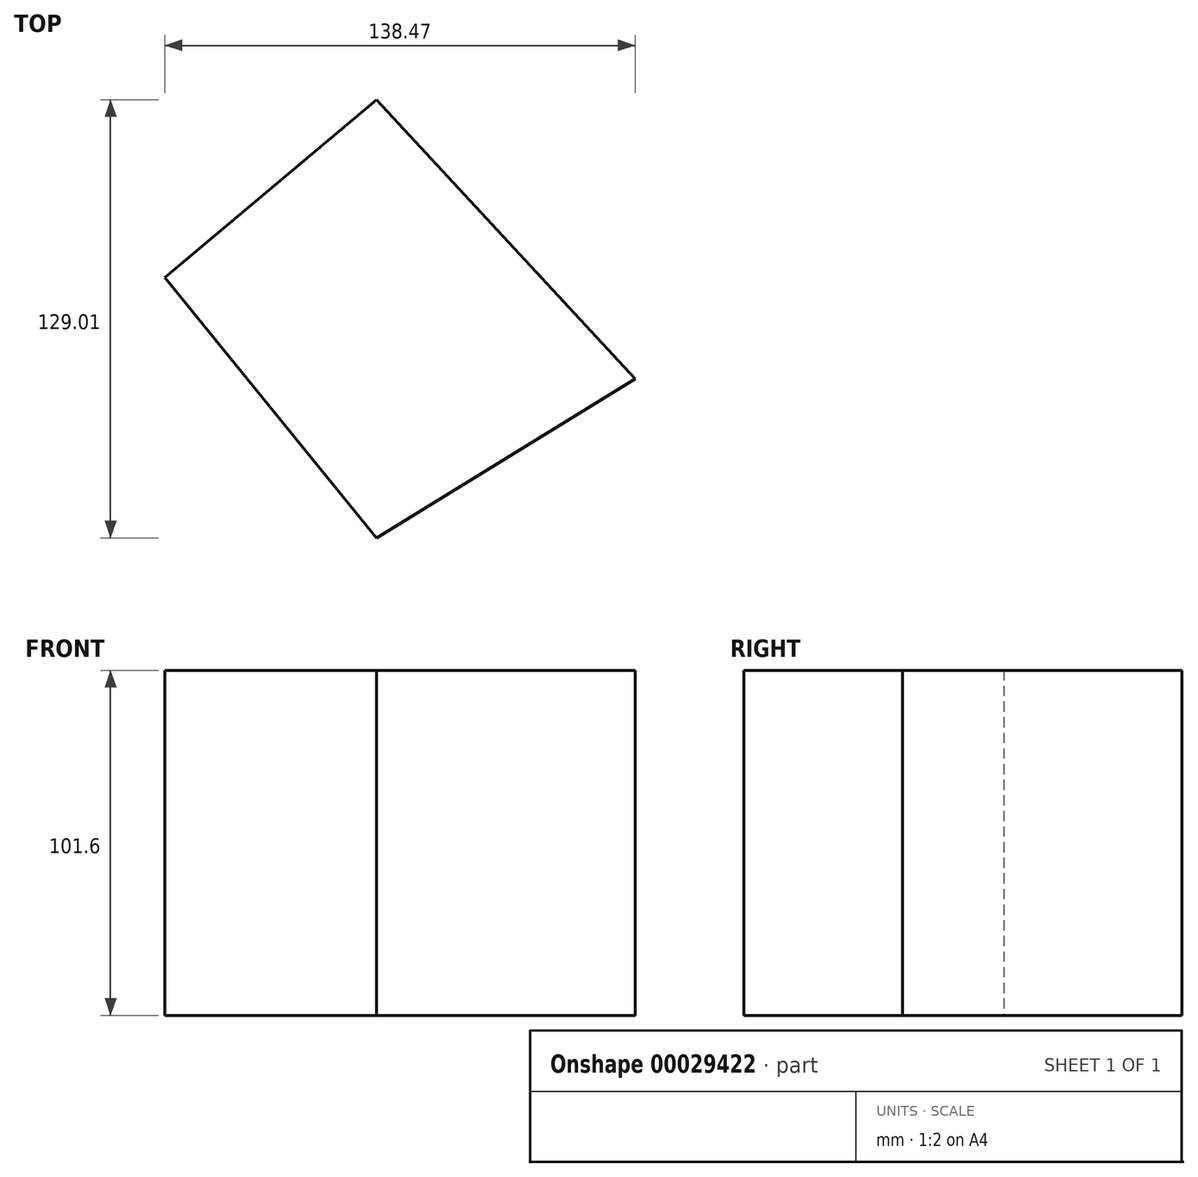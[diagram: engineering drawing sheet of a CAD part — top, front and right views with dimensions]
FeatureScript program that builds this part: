
annotation { "Feature Type Name" : "Feature", "Feature Type Description" : "" }
export const myFeature = defineFeature(function(context is Context, id is Id, definition is map)
    precondition{}
    {
        {
            var Q0;
            Q0=qCreatedBy(makeId("Top.planeOp"),FACE);
            var sketch = newSketch(context, id + "F0", { "sketchPlane" : qUnion([Q0])});
            skLineSegment(sketch, "E0", {"start": v(-62.28, 0) * mm, "end": v(0, 52.33) * mm});
            skLineSegment(sketch, "E1", {"start": v(0, 52.33) * mm, "end": v(76.19, -29.84) * mm});
            skLineSegment(sketch, "E2", {"start": v(76.19, -29.84) * mm, "end": v(0, -76.68) * mm});
            skLineSegment(sketch, "E3", {"start": v(0, -76.68) * mm, "end": v(-62.28, 0) * mm});
            skSolve(sketch);
        }
        {
            var Q0;
            Q0 = qSketchRegion(id + "F0", true);
            extrude(context, id + "F1", {"entities" : qUnion([Q0]), "depth" : 101.6 * mm});
        }
    });
